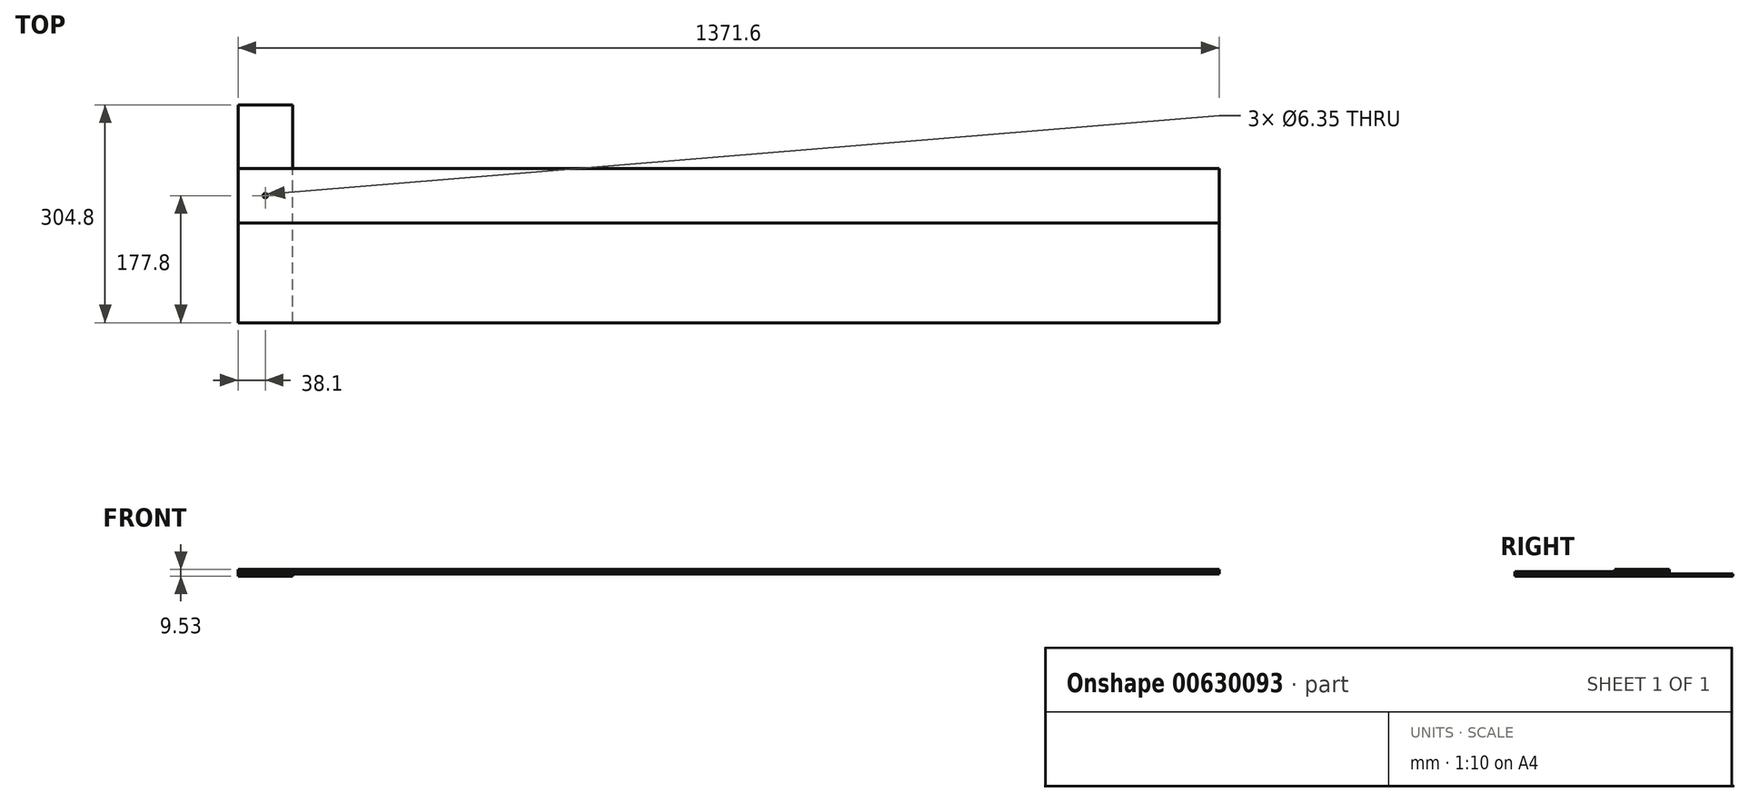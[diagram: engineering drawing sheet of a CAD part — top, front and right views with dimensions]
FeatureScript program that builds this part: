
annotation { "Feature Type Name" : "Feature", "Feature Type Description" : "" }
export const myFeature = defineFeature(function(context is Context, id is Id, definition is map)
    precondition{}
    {
        {
            var Q0;
            Q0=qCreatedBy(makeId("Top.planeOp"),FACE);
            var sketch = newSketch(context, id + "F0", { "sketchPlane" : qUnion([Q0])});
            skLineSegment(sketch, "E0.bottom", {"start": v(685.8, 107.95) * mm, "end": v(-685.8, 107.95) * mm});
            skLineSegment(sketch, "E0.top", {"start": v(685.8, -107.95) * mm, "end": v(-685.8, -107.95) * mm});
            skLineSegment(sketch, "E0.left", {"start": v(685.8, 107.95) * mm, "end": v(685.8, -107.95) * mm});
            skLineSegment(sketch, "E0.right", {"start": v(-685.8, 107.95) * mm, "end": v(-685.8, -107.95) * mm});
            skPoint(sketch, "E0.middle", {"position": v(0, 0) * mm});
            skSolve(sketch);
        }
        {
            var Q0;
            Q0 = qSketchRegion(id + "F0", true);
            extrude(context, id + "F1", {"entities" : qUnion([Q0]), "depth" : 3.17 * mm, "offsetDistance" : 25.4 * mm});
        }
        {
            var Q0;
            Q0=makeQuery(id+"F1.opExtrude","CAP_FACE",FACE,{"disambiguationData":[OSD([sQuery(id+"F0.wireOp",EDGE,"E0.bottom"),sQuery(id+"F0.wireOp",EDGE,"E0.top"),sQuery(id+"F0.wireOp",EDGE,"E0.left"),sQuery(id+"F0.wireOp",EDGE,"E0.right")])],"isStart":false});
            var sketch = newSketch(context, id + "F2", { "sketchPlane" : qUnion([Q0])});
            skLineSegment(sketch, "E1.bottom", {"start": v(-685.8, 107.95) * mm, "end": v(685.8, 107.95) * mm});
            skLineSegment(sketch, "E1.top", {"start": v(-685.8, 31.75) * mm, "end": v(685.8, 31.75) * mm});
            skLineSegment(sketch, "E1.left", {"start": v(-685.8, 107.95) * mm, "end": v(-685.8, 31.75) * mm});
            skLineSegment(sketch, "E1.right", {"start": v(685.8, 107.95) * mm, "end": v(685.8, 31.75) * mm});
            skSolve(sketch);
        }
        {
            var Q0;
            Q0 = qSketchRegion(id + "F2", true);
            extrude(context, id + "F3", {"entities" : qUnion([Q0]), "depth" : 3.17 * mm, "offsetDistance" : 25.4 * mm});
        }
        {
            var Q0;
            Q0=makeQuery(id+"F1.opExtrude","CAP_FACE",FACE,{"disambiguationData":[OSD([sQuery(id+"F0.wireOp",EDGE,"E0.bottom"),sQuery(id+"F0.wireOp",EDGE,"E0.top"),sQuery(id+"F0.wireOp",EDGE,"E0.left"),sQuery(id+"F0.wireOp",EDGE,"E0.right")])],"isStart":true});
            var sketch = newSketch(context, id + "F4", { "sketchPlane" : qUnion([Q0])});
            skLineSegment(sketch, "E2.bottom", {"start": v(-685.8, 107.95) * mm, "end": v(-609.6, 107.95) * mm});
            skLineSegment(sketch, "E2.top", {"start": v(-685.8, -196.85) * mm, "end": v(-609.6, -196.85) * mm});
            skLineSegment(sketch, "E2.left", {"start": v(-685.8, 107.95) * mm, "end": v(-685.8, -196.85) * mm});
            skLineSegment(sketch, "E2.right", {"start": v(-609.6, 107.95) * mm, "end": v(-609.6, -196.85) * mm});
            skSolve(sketch);
        }
        {
            var Q0;
            Q0 = qSketchRegion(id + "F4", true);
            extrude(context, id + "F5", {"entities" : qUnion([Q0]), "depth" : 3.17 * mm, "offsetDistance" : 25.4 * mm});
        }
        {
            var Q0;
            Q0=makeQuery(id+"F3.opExtrude","CAP_FACE",FACE,{"disambiguationData":[OSD([sQuery(id+"F2.wireOp",EDGE,"E1.bottom"),sQuery(id+"F2.wireOp",EDGE,"E1.top"),sQuery(id+"F2.wireOp",EDGE,"E1.left"),sQuery(id+"F2.wireOp",EDGE,"E1.right")])],"isStart":false});
            var sketch = newSketch(context, id + "F6", { "sketchPlane" : qUnion([Q0])});
            skPoint(sketch, "E3.0", {"position": v(-685.8, 107.95) * mm});
            skPoint(sketch, "E4.0", {"position": v(-647.7, 196.85) * mm});
            skPoint(sketch, "E5", {"position": v(-685.8, 69.85) * mm});
            skLineSegment(sketch, "E6", {"start": v(-685.8, 69.85) * mm, "end": v(685.8, 69.85) * mm, "construction": true});
            skLineSegment(sketch, "E7", {"start": v(-647.7, 196.85) * mm, "end": v(-647.7, -109.65) * mm, "construction": true});
            skCircle(sketch, "E8", {"center": v(-647.7, 69.85) * mm, "radius": 3.18 * mm});
            skSolve(sketch);
        }
        {
            var Q0;
            Q0=makeQuery(id+"F6.imprint","IMPRINT",FACE,{"disambiguationData":[TD([[makeQuery(id+"F6.imprint","IMPRINT",EDGE,{"derivedFrom":sQuery(id+"F6.wireOp",EDGE,"E8")}),-1.0]])]});
            var sketch = newSketch(context, id + "F7", { "sketchPlane" : qUnion([Q0])});
            skSolve(sketch);
        }
        {
            var Q0;
            Q0 = qSketchRegion(id + "F6", true);
            extrude(context, id + "F8", {"entities" : qUnion([Q0]), "operationType" : NewBodyOperationType.REMOVE, "endBound" : BoundingType.THROUGH_ALL, "oppositeDirection" : true, "depth" : 25.4 * mm, "offsetDistance" : 25.4 * mm});
        }
    });
